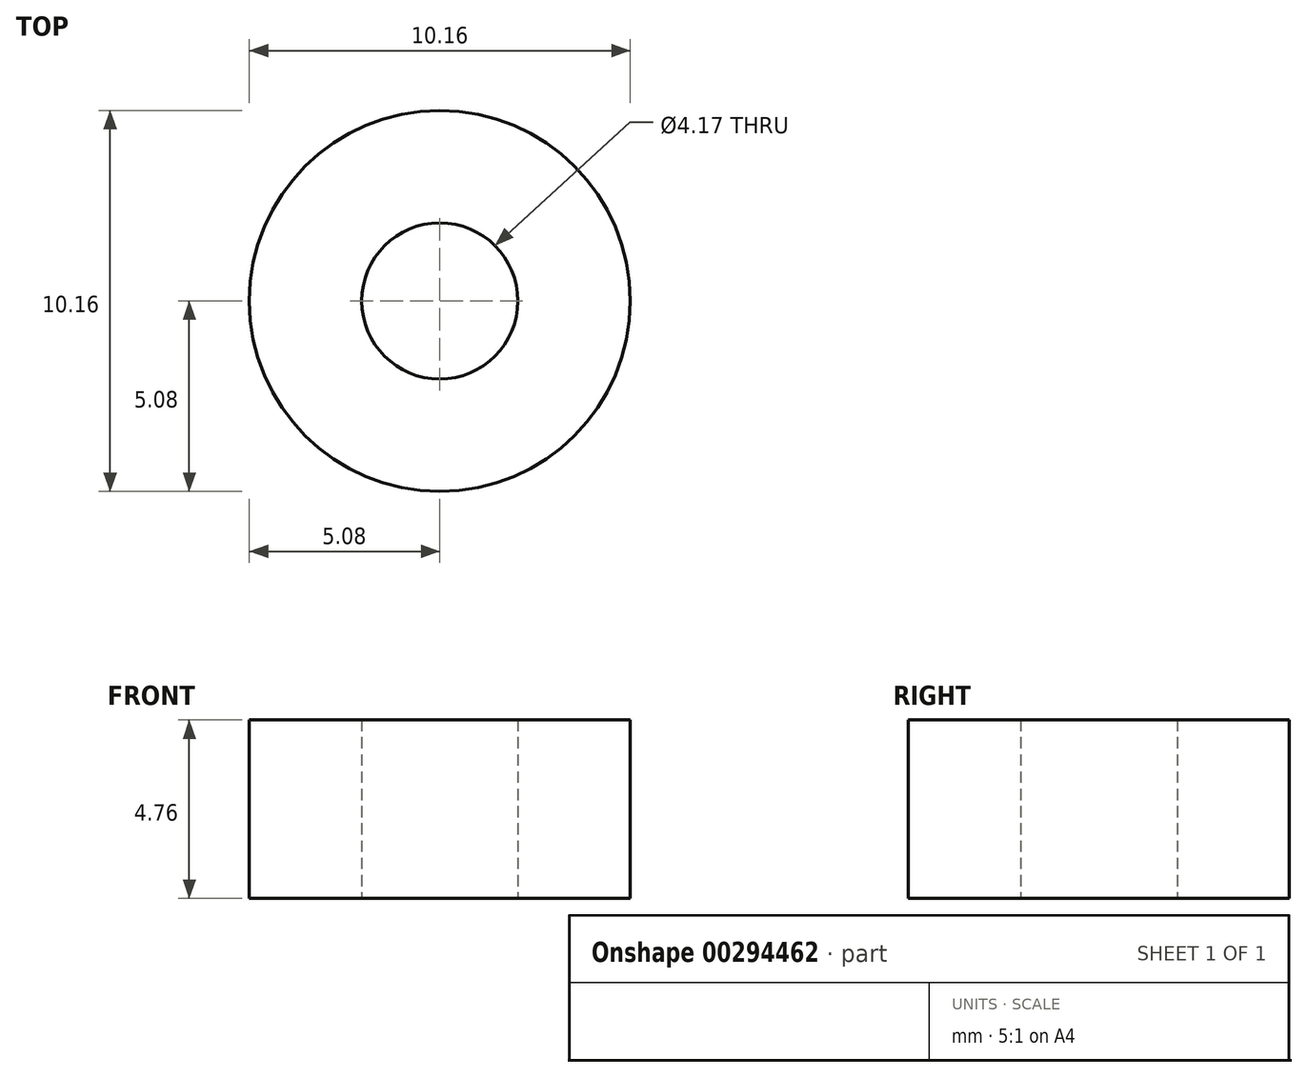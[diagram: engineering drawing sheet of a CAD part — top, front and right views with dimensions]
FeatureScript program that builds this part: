
annotation { "Feature Type Name" : "Feature", "Feature Type Description" : "" }
export const myFeature = defineFeature(function(context is Context, id is Id, definition is map)
    precondition{}
    {
        {
            var Q0;
            Q0=qCreatedBy(makeId("Top.planeOp"),FACE);
            var sketch = newSketch(context, id + "F0", { "sketchPlane" : qUnion([Q0])});
            skCircle(sketch, "E0", {"center": v(0, 0) * mm, "radius": 5.08 * mm});
            skCircle(sketch, "E1", {"center": v(0, 0) * mm, "radius": 2.08 * mm});
            skSolve(sketch);
        }
        {
            var Q0;
            Q0=makeQuery(id+"F0.imprint","IMPRINT",FACE,{"disambiguationData":[TD([[makeQuery(id+"F0.imprint","IMPRINT",EDGE,{"derivedFrom":sQuery(id+"F0.wireOp",EDGE,"E0")}),1.0]])]});
            extrude(context, id + "F1", {"entities" : qUnion([Q0]), "depth" : 4.76 * mm});
        }
    });
